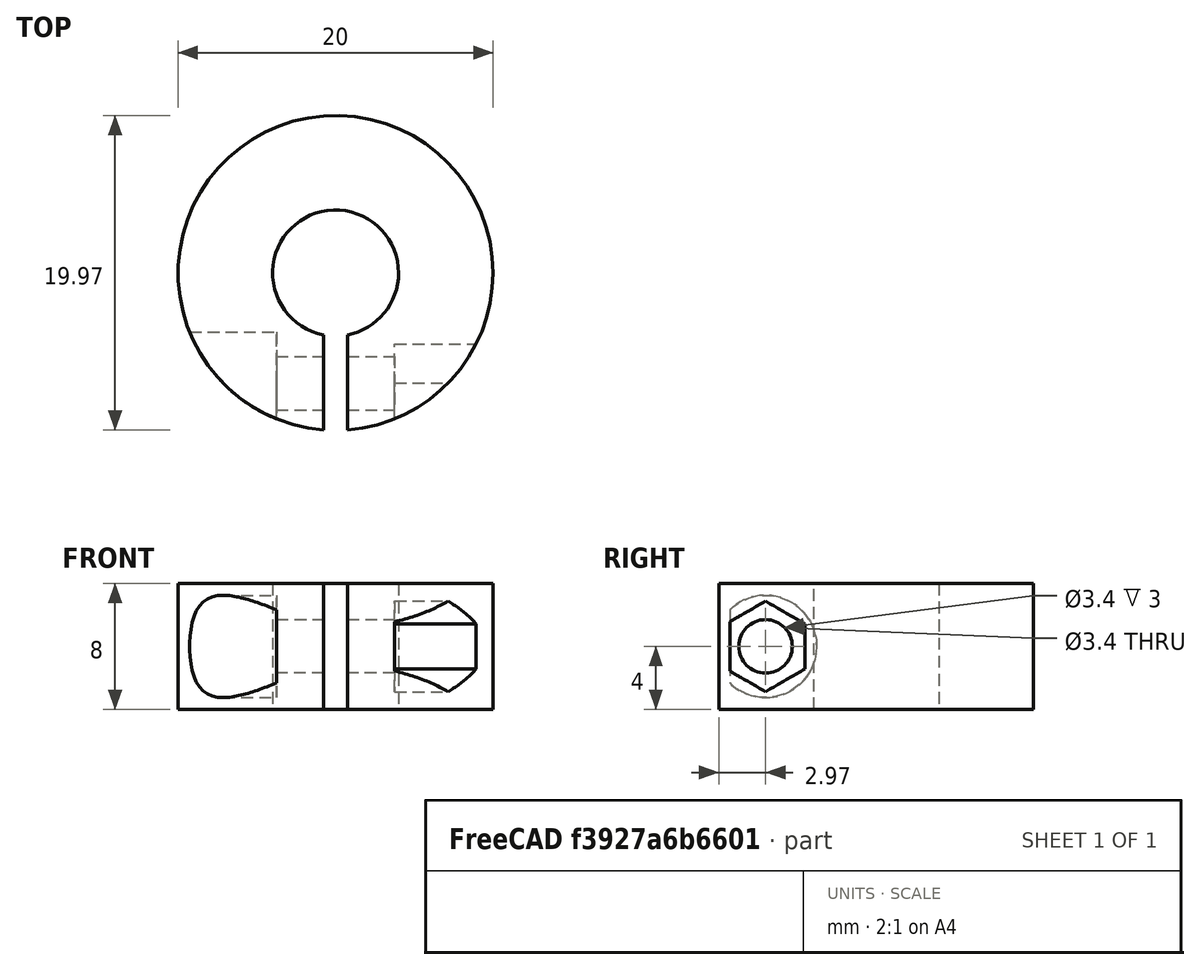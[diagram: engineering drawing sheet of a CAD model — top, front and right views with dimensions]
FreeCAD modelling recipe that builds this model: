
FCSTD DOCUMENT  (FreeCAD 0.19R17798 (Git))
Label: shaftcollar8mm
License: All rights reserved
LicenseURL: http://en.wikipedia.org/wiki/All_rights_reserved
objects: Part::Part2DObjectPython×4, Part::FeaturePython×4, Part::Extrusion×4, Part::Cut×2, Part::Plane×1, Part::Fuse×1, Part::Feature×1, Part::Mirroring×1, Part::MultiFuse×1
note: 19 computed .brp shape members not serialized (recipe doc carries the construction recipe); baked Part::Feature solids carry a one-line shape summary decoded from their .brp

FEATURE [Part::Part2DObjectPython] circle  # Draft 2D object (typed FeaturePython)
  Area = 314.159
  FirstAngle = 0
  LastAngle = 0
  MakeFace = true
  Radius = 10
FEATURE [Part::Part2DObjectPython] circle001  # Draft 2D object (typed FeaturePython)
  Area = 50.2655
  FirstAngle = 0
  LastAngle = 0
  MakeFace = true
  Radius = 4
FEATURE [Part::Plane] square
  AttacherType = Attacher::AttachEngine3D
  Length = 1.5
  Placement = pos=(-0.75,-40,0) rot=(0,0,1;0rad)
  Width = 40
FEATURE [Part::Fuse] union
  Base = -> circle001
  Refine = true
  Tool = -> square
FEATURE [Part::Cut] difference
  Base = -> circle
  Refine = true
  Tool = -> union
FEATURE [Part::FeaturePython] RefineLinearExtrude  # WARN: FeaturePython — macro-defined, semantics opaque (R4)
  Base = -> difference
FEATURE [Part::Extrusion] LinearExtrude
  Base = -> RefineLinearExtrude
  Dir = (0,0,8)
  DirMode = 0
  FaceMakerClass = Part::FaceMakerBullseye
  LengthFwd = 0
  LengthRev = 0
  Solid = false
  Symmetric = false
FEATURE [Part::Part2DObjectPython] circle002  # Draft 2D object (typed FeaturePython)
  Area = 9.0792
  FirstAngle = 0
  LastAngle = 0
  MakeFace = true
  Radius = 1.7
FEATURE [Part::FeaturePython] RefineLinearExtrude001  # WARN: FeaturePython — macro-defined, semantics opaque (R4)
  Base = -> circle002
FEATURE [Part::Extrusion] LinearExtrude001
  Base = -> RefineLinearExtrude001
  Dir = (0,0,20)
  DirMode = 0
  FaceMakerClass = Part::FaceMakerBullseye
  LengthFwd = 0
  LengthRev = 0
  Placement = pos=(0,0,-10) rot=(0,0,1;0rad)
  Solid = false
  Symmetric = false
FEATURE [Part::Part2DObjectPython] circle003  # Draft 2D object (typed FeaturePython)
  Area = 33.1831
  FirstAngle = 0
  LastAngle = 0
  MakeFace = true
  Radius = 3.25
FEATURE [Part::FeaturePython] RefineLinearExtrude002  # WARN: FeaturePython — macro-defined, semantics opaque (R4)
  Base = -> circle003
FEATURE [Part::Extrusion] LinearExtrude002
  Base = -> RefineLinearExtrude002
  Dir = (0,0,100)
  DirMode = 0
  FaceMakerClass = Part::FaceMakerBullseye
  LengthFwd = 0
  LengthRev = 0
  Placement = pos=(0,0,3.75) rot=(0,0,1;0rad)
  Solid = false
  Symmetric = false
FEATURE [Part::Feature] polygon
  shape: bbox 5.75 x 4.98 x 2e-07 mm, 1 faces, 0 solids (baked)
FEATURE [Part::FeaturePython] RefineLinearExtrude003  # WARN: FeaturePython — macro-defined, semantics opaque (R4)
  Base = -> polygon
FEATURE [Part::Extrusion] LinearExtrude003
  Base = -> RefineLinearExtrude003
  Dir = (0,0,100)
  DirMode = 0
  FaceMakerClass = Part::FaceMakerBullseye
  LengthFwd = 0
  LengthRev = 0
  Placement = pos=(0,0,3.75) rot=(0,0,1;0rad)
  Solid = false
  Symmetric = false
FEATURE [Part::Mirroring] mirr_LinearExtrude003  label="mirrored LinearExtrude003"
  Base = (0,0,0)
  Normal = (0,0,1)
  Source = -> LinearExtrude003
FEATURE [Part::MultiFuse] union001
  Placement = pos=(0,-7,4) rot=(0.707107,0,-0.707107;3.14159rad)
  Refine = true
  Shapes = -> [LinearExtrude001,LinearExtrude002,mirr_LinearExtrude003]
FEATURE [Part::Cut] difference001
  Base = -> LinearExtrude
  Refine = true
  Tool = -> union001
